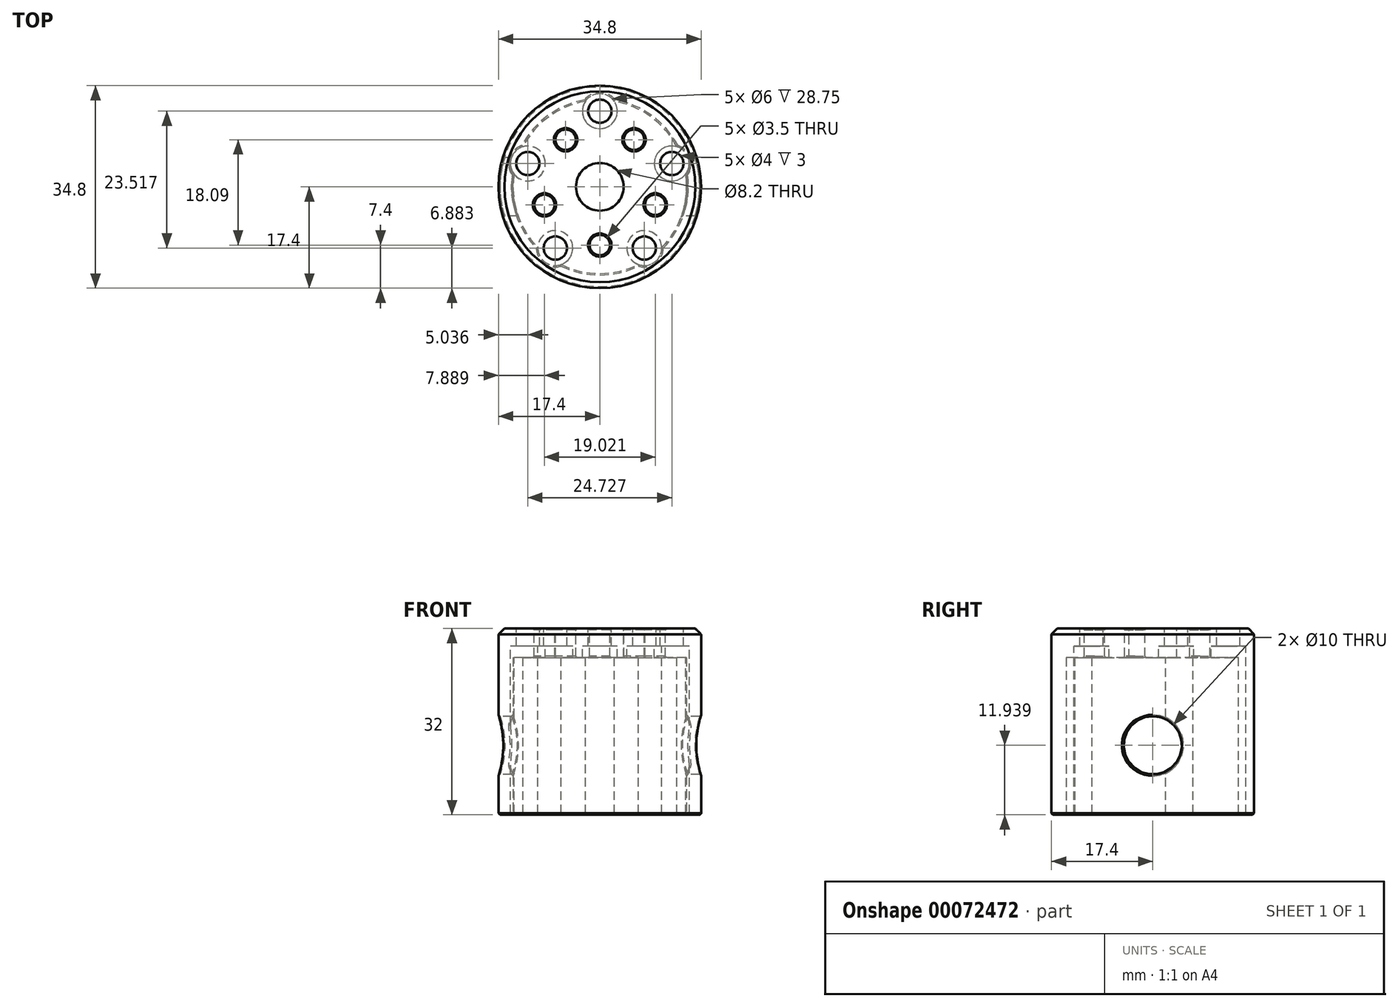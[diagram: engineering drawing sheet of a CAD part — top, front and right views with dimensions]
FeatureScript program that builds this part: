
annotation { "Feature Type Name" : "Feature", "Feature Type Description" : "" }
export const myFeature = defineFeature(function(context is Context, id is Id, definition is map)
    precondition{}
    {
        {
            var Q0;
            Q0=qCreatedBy(makeId("Top.planeOp"),FACE);
            var sketch = newSketch(context, id + "F0", { "sketchPlane" : qUnion([Q0])});
            skCircle(sketch, "E0", {"center": v(0, 0) * mm, "radius": 17.4 * mm});
            skSolve(sketch);
        }
        {
            var Q0;
            Q0=makeQuery(id+"F0.imprint","IMPRINT",FACE,{"disambiguationData":[TD([[makeQuery(id+"F0.imprint","IMPRINT",EDGE,{"derivedFrom":sQuery(id+"F0.wireOp",EDGE,"E0")}),1.0]])]});
            extrude(context, id + "F1", {"entities" : qUnion([Q0]), "depth" : 32 * mm});
        }
        {
            var Q0;
            Q0=makeQuery(id+"F1.opExtrude","CAP_FACE",FACE,{"disambiguationData":[OSD([sQuery(id+"F0.wireOp",EDGE,"E0")])],"isStart":true});
            var sketch = newSketch(context, id + "F2", { "sketchPlane" : qUnion([Q0])});
            skCircle(sketch, "E1", {"center": v(0, 0) * mm, "radius": 14.9 * mm});
            skSolve(sketch);
        }
        {
            var Q0;
            Q0=makeQuery(id+"F2.imprint","IMPRINT",FACE,{"disambiguationData":[TD([[makeQuery(id+"F2.imprint","IMPRINT",EDGE,{"derivedFrom":sQuery(id+"F2.wireOp",EDGE,"E1")}),1.0]])]});
            extrude(context, id + "F3", {"entities" : qUnion([Q0]), "operationType" : NewBodyOperationType.REMOVE, "oppositeDirection" : true, "depth" : 27 * mm});
        }
        {
            var Q0;
            Q0=makeQuery(id+"F1.opExtrude","CAP_FACE",FACE,{"disambiguationData":[OSD([sQuery(id+"F0.wireOp",EDGE,"E0")])],"isStart":false});
            var sketch = newSketch(context, id + "F4", { "sketchPlane" : qUnion([Q0])});
            skCircle(sketch, "E2", {"center": v(0, 0) * mm, "radius": 4.1 * mm});
            skCircle(sketch, "E3", {"center": v(0, 0) * mm, "radius": 14.9 * mm, "construction": true});
            skLineSegment(sketch, "E4", {"start": v(0, 0) * mm, "end": v(0, -10) * mm, "construction": true});
            skCircle(sketch, "E5", {"center": v(0, -10) * mm, "radius": 1.75 * mm});
            skCircle(sketch, "E6.1.0", {"center": v(9.51, -3.1) * mm, "radius": 1.75 * mm});
            skCircle(sketch, "E6.2.0", {"center": v(5.88, 8.1) * mm, "radius": 1.75 * mm});
            skCircle(sketch, "E6.3.0", {"center": v(-5.88, 8.1) * mm, "radius": 1.75 * mm});
            skCircle(sketch, "E6.4.0", {"center": v(-9.51, -3.1) * mm, "radius": 1.75 * mm});
            skSolve(sketch);
        }
        {
            var Q0;
            Q0=makeQuery(id+"F4.imprint","IMPRINT",FACE,{"disambiguationData":[TD([[makeQuery(id+"F4.imprint","IMPRINT",EDGE,{"derivedFrom":sQuery(id+"F4.wireOp",EDGE,"E6.1.0")}),1.0]])]});
            var Q1;
            Q1=makeQuery(id+"F4.imprint","IMPRINT",FACE,{"disambiguationData":[TD([[makeQuery(id+"F4.imprint","IMPRINT",EDGE,{"derivedFrom":sQuery(id+"F4.wireOp",EDGE,"E5")}),1.0]])]});
            var Q2;
            Q2=makeQuery(id+"F4.imprint","IMPRINT",FACE,{"disambiguationData":[TD([[makeQuery(id+"F4.imprint","IMPRINT",EDGE,{"derivedFrom":sQuery(id+"F4.wireOp",EDGE,"E6.4.0")}),1.0]])]});
            var Q3;
            Q3=makeQuery(id+"F4.imprint","IMPRINT",FACE,{"disambiguationData":[TD([[makeQuery(id+"F4.imprint","IMPRINT",EDGE,{"derivedFrom":sQuery(id+"F4.wireOp",EDGE,"E6.3.0")}),1.0]])]});
            var Q4;
            Q4=makeQuery(id+"F4.imprint","IMPRINT",FACE,{"disambiguationData":[TD([[makeQuery(id+"F4.imprint","IMPRINT",EDGE,{"derivedFrom":sQuery(id+"F4.wireOp",EDGE,"E6.2.0")}),1.0]])]});
            var Q5;
            Q5=makeQuery(id+"F4.imprint","IMPRINT",FACE,{"disambiguationData":[TD([[makeQuery(id+"F4.imprint","IMPRINT",EDGE,{"derivedFrom":sQuery(id+"F4.wireOp",EDGE,"E2")}),1.0]])]});
            extrude(context, id + "F5", {"entities" : qUnion([Q0, Q1, Q2, Q3, Q4, Q5]), "operationType" : NewBodyOperationType.REMOVE, "endBound" : BoundingType.THROUGH_ALL, "oppositeDirection" : true, "depth" : 25 * mm});
        }
        {
            var Q0;
            Q0=makeQuery(id+"F1.opExtrude","CAP_FACE",FACE,{"disambiguationData":[OSD([sQuery(id+"F0.wireOp",EDGE,"E0")])],"isStart":false});
            var sketch = newSketch(context, id + "F6", { "sketchPlane" : qUnion([Q0])});
            skCircle(sketch, "E7", {"center": v(0, 0) * mm, "radius": 13 * mm, "construction": true});
            skLineSegment(sketch, "E8", {"start": v(0, -10) * mm, "end": v(-9.51, -3.1) * mm, "construction": true});
            skLineSegment(sketch, "E9", {"start": v(0, 0) * mm, "end": v(-7.64, -10.52) * mm, "construction": true});
            skCircle(sketch, "E10", {"center": v(-7.64, -10.52) * mm, "radius": 2 * mm});
            skCircle(sketch, "E11", {"center": v(-7.64, -10.52) * mm, "radius": 3 * mm});
            skCircle(sketch, "E12.1.0", {"center": v(7.64, -10.52) * mm, "radius": 2 * mm});
            skCircle(sketch, "E12.1.1", {"center": v(7.64, -10.52) * mm, "radius": 3 * mm});
            skCircle(sketch, "E12.2.0", {"center": v(12.36, 4.02) * mm, "radius": 2 * mm});
            skCircle(sketch, "E12.2.1", {"center": v(12.36, 4.02) * mm, "radius": 3 * mm});
            skCircle(sketch, "E13.1.3.0", {"center": v(0, 13) * mm, "radius": 2 * mm});
            skCircle(sketch, "E13.2.3.0", {"center": v(0, 13) * mm, "radius": 3 * mm});
            skCircle(sketch, "E13.1.4.0", {"center": v(-12.36, 4.02) * mm, "radius": 2 * mm});
            skCircle(sketch, "E13.2.4.0", {"center": v(-12.36, 4.02) * mm, "radius": 3 * mm});
            skSolve(sketch);
        }
        {
            var Q0;
            Q0=makeQuery(id+"F6.imprint","IMPRINT",FACE,{"disambiguationData":[TD([[makeQuery(id+"F6.imprint","IMPRINT",EDGE,{"derivedFrom":sQuery(id+"F6.wireOp",EDGE,"E12.1.0")}),1.0]])]});
            var Q1;
            Q1=makeQuery(id+"F6.imprint","IMPRINT",FACE,{"disambiguationData":[TD([[makeQuery(id+"F6.imprint","IMPRINT",EDGE,{"derivedFrom":sQuery(id+"F6.wireOp",EDGE,"E10")}),1.0]])]});
            var Q2;
            Q2=makeQuery(id+"F6.imprint","IMPRINT",FACE,{"disambiguationData":[TD([[makeQuery(id+"F6.imprint","IMPRINT",EDGE,{"derivedFrom":sQuery(id+"F6.wireOp",EDGE,"E13.1.4.0")}),1.0]])]});
            var Q3;
            Q3=makeQuery(id+"F6.imprint","IMPRINT",FACE,{"disambiguationData":[TD([[makeQuery(id+"F6.imprint","IMPRINT",EDGE,{"derivedFrom":sQuery(id+"F6.wireOp",EDGE,"E13.1.3.0")}),1.0]])]});
            var Q4;
            Q4=makeQuery(id+"F6.imprint","IMPRINT",FACE,{"disambiguationData":[TD([[makeQuery(id+"F6.imprint","IMPRINT",EDGE,{"derivedFrom":sQuery(id+"F6.wireOp",EDGE,"E12.2.0")}),1.0]])]});
            extrude(context, id + "F7", {"entities" : qUnion([Q0, Q1, Q2, Q3, Q4]), "operationType" : NewBodyOperationType.REMOVE, "endBound" : BoundingType.THROUGH_ALL, "oppositeDirection" : true, "depth" : 25 * mm});
        }
        {
            var Q0;
            Q0=makeQuery(id+"F6.imprint","IMPRINT",FACE,{"disambiguationData":[TD([[makeQuery(id+"F6.imprint","IMPRINT",EDGE,{"derivedFrom":sQuery(id+"F6.wireOp",EDGE,"E12.1.0")}),-1.0]])]});
            var Q1;
            Q1=makeQuery(id+"F6.imprint","IMPRINT",FACE,{"disambiguationData":[TD([[makeQuery(id+"F6.imprint","IMPRINT",EDGE,{"derivedFrom":sQuery(id+"F6.wireOp",EDGE,"E10")}),-1.0]])]});
            var Q2;
            Q2=makeQuery(id+"F6.imprint","IMPRINT",FACE,{"disambiguationData":[TD([[makeQuery(id+"F6.imprint","IMPRINT",EDGE,{"derivedFrom":sQuery(id+"F6.wireOp",EDGE,"E13.1.4.0")}),-1.0]])]});
            var Q3;
            Q3=makeQuery(id+"F6.imprint","IMPRINT",FACE,{"disambiguationData":[TD([[makeQuery(id+"F6.imprint","IMPRINT",EDGE,{"derivedFrom":sQuery(id+"F6.wireOp",EDGE,"E13.1.3.0")}),-1.0]])]});
            var Q4;
            Q4=makeQuery(id+"F6.imprint","IMPRINT",FACE,{"disambiguationData":[TD([[makeQuery(id+"F6.imprint","IMPRINT",EDGE,{"derivedFrom":sQuery(id+"F6.wireOp",EDGE,"E12.2.0")}),-1.0]])]});
            extrude(context, id + "F8", {"entities" : qUnion([Q0, Q1, Q2, Q3, Q4]), "operationType" : NewBodyOperationType.REMOVE, "oppositeDirection" : true, "depth" : 35 * mm, "hasSecondDirection" : true, "secondDirectionOppositeDirection" : true, "secondDirectionDepth" : 3 * mm});
        }
        {
            var Q0;
            Q0=qCreatedBy(makeId("Right.planeOp"),FACE);
            var sketch = newSketch(context, id + "F9", { "sketchPlane" : qUnion([Q0])});
            skLineSegment(sketch, "E14", {"start": v(0, 31.94) * mm, "end": v(0, 11.94) * mm, "construction": true});
            skCircle(sketch, "E15", {"center": v(0, 11.94) * mm, "radius": 5 * mm});
            skSolve(sketch);
        }
        {
            var Q0;
            Q0=makeQuery(id+"F9.imprint","IMPRINT",FACE,{"disambiguationData":[TD([[makeQuery(id+"F9.imprint","IMPRINT",EDGE,{"derivedFrom":sQuery(id+"F9.wireOp",EDGE,"E15")}),1.0]])]});
            extrude(context, id + "F10", {"entities" : qUnion([Q0]), "operationType" : NewBodyOperationType.REMOVE, "depth" : 40 * mm, "symmetric" : true});
        }
        {
            var Q0;
            Q0=makeQuery(id+"F1.opExtrude","CAP_EDGE",EDGE,{"disambiguationData":[OSD([sQuery(id+"F0.wireOp",EDGE,"E0")])],"isStart":false});
            chamfer(context, id + "F11", {"entities" : qUnion([Q0]), "width" : 1 * mm, "tangentPropagation" : true});
        }
        {
            var Q0;
            Q0=makeQuery(id+"F5.boolean.opBoolean","COPY",FACE,{"derivedFrom":makeQuery(id+"F5.opExtrude","SWEPT_FACE",FACE,{"disambiguationData":[OSD([sQuery(id+"F4.wireOp",EDGE,"E6.3.0")])]})});
            var Q1;
            Q1=makeQuery(id+"F5.boolean.opBoolean","COPY",FACE,{"derivedFrom":makeQuery(id+"F5.opExtrude","SWEPT_FACE",FACE,{"disambiguationData":[OSD([sQuery(id+"F4.wireOp",EDGE,"E6.4.0")])]})});
            var Q2;
            Q2=makeQuery(id+"F5.boolean.opBoolean","COPY",FACE,{"derivedFrom":makeQuery(id+"F5.opExtrude","SWEPT_FACE",FACE,{"disambiguationData":[OSD([sQuery(id+"F4.wireOp",EDGE,"E5")])]})});
            var Q3;
            Q3=makeQuery(id+"F5.boolean.opBoolean","COPY",FACE,{"derivedFrom":makeQuery(id+"F5.opExtrude","SWEPT_FACE",FACE,{"disambiguationData":[OSD([sQuery(id+"F4.wireOp",EDGE,"E6.1.0")])]})});
            var Q4;
            Q4=makeQuery(id+"F5.boolean.opBoolean","COPY",FACE,{"derivedFrom":makeQuery(id+"F5.opExtrude","SWEPT_FACE",FACE,{"disambiguationData":[OSD([sQuery(id+"F4.wireOp",EDGE,"E6.2.0")])]})});
            chamfer(context, id + "F12", {"entities" : qUnion([Q0, Q1, Q2, Q3, Q4]), "width" : .25 * mm, "tangentPropagation" : true});
        }
        {
            var Q0;
            Q0=makeQuery(id+"F10.boolean.opBoolean","COPY",FACE,{"disambiguationData":[TD([makeQuery(id+"F8.boolean.opBoolean","COPY",FACE,{"derivedFrom":makeQuery(id+"F8.opExtrude","SWEPT_FACE",FACE,{"disambiguationData":[OSD([sQuery(id+"F6.wireOp",EDGE,"E12.2.1")])]})})])],"derivedFrom":makeQuery(id+"F10.opExtrude","SWEPT_FACE",FACE,{"disambiguationData":[OSD([sQuery(id+"F9.wireOp",EDGE,"E15")])]})});
            var Q1;
            Q1=makeQuery(id+"F10.boolean.opBoolean","COPY",FACE,{"disambiguationData":[TD([makeQuery(id+"F8.boolean.opBoolean","COPY",FACE,{"derivedFrom":makeQuery(id+"F8.opExtrude","SWEPT_FACE",FACE,{"disambiguationData":[OSD([sQuery(id+"F6.wireOp",EDGE,"E13.2.4.0")])]})})])],"derivedFrom":makeQuery(id+"F10.opExtrude","SWEPT_FACE",FACE,{"disambiguationData":[OSD([sQuery(id+"F9.wireOp",EDGE,"E15")])]})});
            chamfer(context, id + "F13", {"entities" : qUnion([Q0, Q1]), "width" : .25 * mm, "tangentPropagation" : true});
        }
        {
            var Q0;
            Q0=makeQuery(id+"F1.opExtrude","CAP_FACE",FACE,{"disambiguationData":[OSD([sQuery(id+"F0.wireOp",EDGE,"E0")])],"isStart":true});
            chamfer(context, id + "F14", {"entities" : qUnion([Q0]), "width" : .25 * mm, "tangentPropagation" : true});
        }
    });
